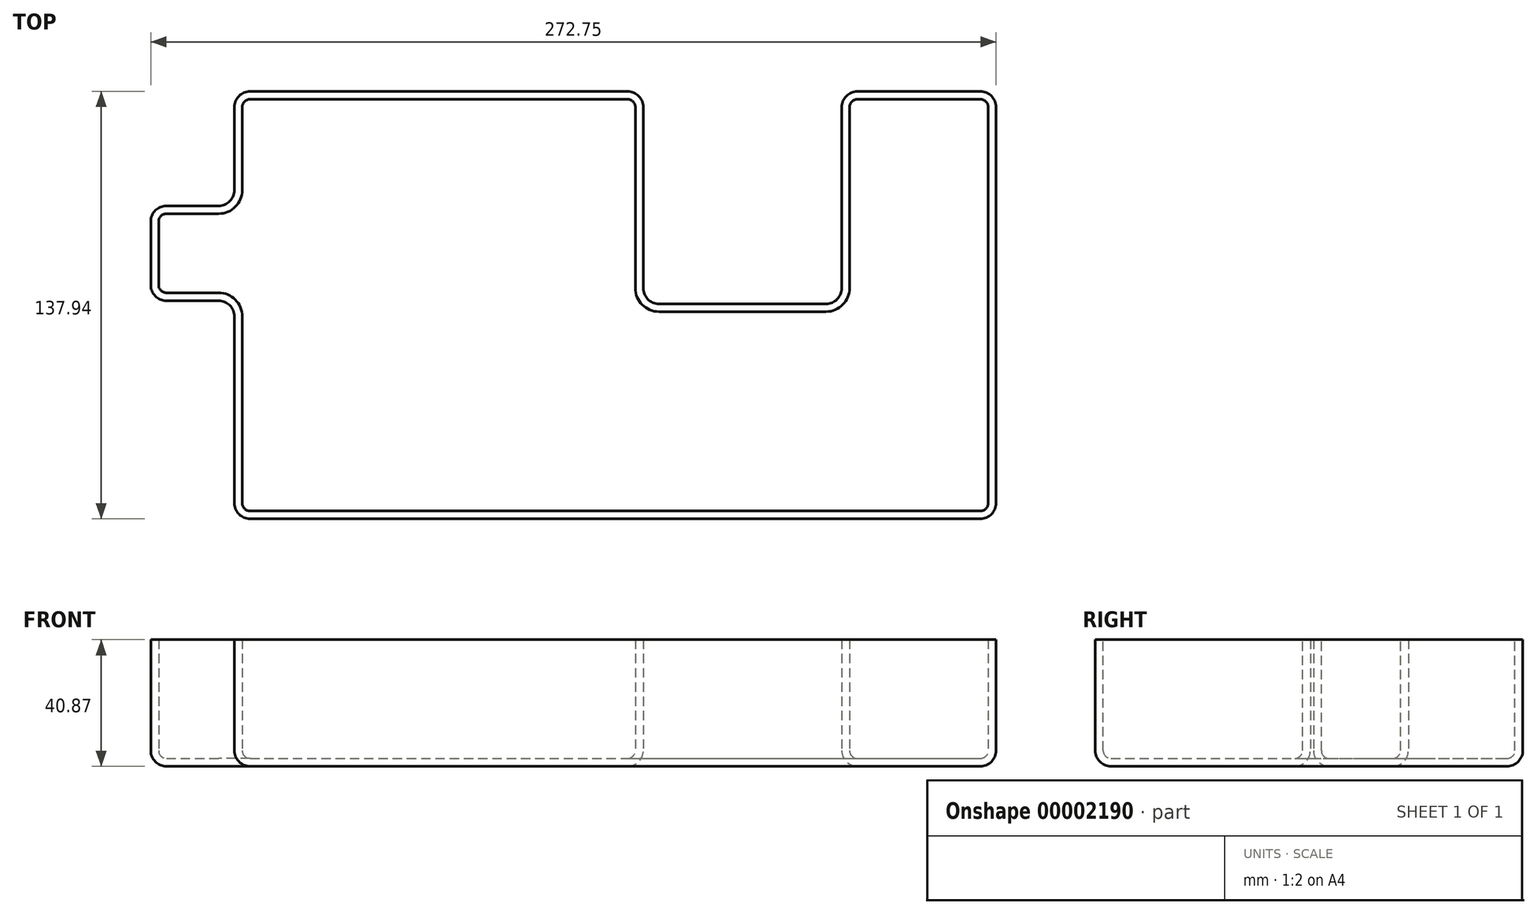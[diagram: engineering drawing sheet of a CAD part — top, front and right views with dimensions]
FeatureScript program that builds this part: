
annotation { "Feature Type Name" : "Feature", "Feature Type Description" : "" }
export const myFeature = defineFeature(function(context is Context, id is Id, definition is map)
    precondition{}
    {
        {
            var Q0;
            Q0=qCreatedBy(makeId("Top.planeOp"),FACE);
            var sketch = newSketch(context, id + "F0", { "sketchPlane" : qUnion([Q0])});
            skLineSegment(sketch, "E0.rect.bottom", {"start": v(-122.9, 68.97) * mm, "end": v(122.9, 68.97) * mm});
            skLineSegment(sketch, "E0.rect.top", {"start": v(-122.9, -68.97) * mm, "end": v(122.9, -68.97) * mm});
            skLineSegment(sketch, "E0.rect.left", {"start": v(-122.9, 68.97) * mm, "end": v(-122.9, -68.97) * mm});
            skLineSegment(sketch, "E0.rect.right", {"start": v(122.9, 68.97) * mm, "end": v(122.9, -68.97) * mm});
            skPoint(sketch, "E0.rect.middle", {"position": v(0, 0) * mm});
            skLineSegment(sketch, "E1.rect.bottom", {"start": v(-149.86, 32.04) * mm, "end": v(-95.92, 32.04) * mm});
            skLineSegment(sketch, "E1.rect.top", {"start": v(-149.86, 1.44) * mm, "end": v(-95.92, 1.44) * mm});
            skLineSegment(sketch, "E1.rect.left", {"start": v(-149.86, 32.04) * mm, "end": v(-149.86, 1.44) * mm});
            skLineSegment(sketch, "E1.rect.right", {"start": v(-95.92, 32.04) * mm, "end": v(-95.92, 1.44) * mm});
            skPoint(sketch, "E1.rect.middle", {"position": v(-122.9, 16.74) * mm});
            skLineSegment(sketch, "E2.rect.bottom", {"start": v(9.03, 113.83) * mm, "end": v(73.09, 113.83) * mm});
            skLineSegment(sketch, "E2.rect.top", {"start": v(9.03, 0.43) * mm, "end": v(73.09, 0.43) * mm});
            skLineSegment(sketch, "E2.rect.left", {"start": v(9.03, 113.83) * mm, "end": v(9.03, 0.43) * mm});
            skLineSegment(sketch, "E2.rect.right", {"start": v(73.09, 113.83) * mm, "end": v(73.09, 0.43) * mm});
            skPoint(sketch, "E2.rect.middle", {"position": v(41.06, 57.13) * mm});
            skSolve(sketch);
        }
        {
            var Q0;
            {var subQ0=sQuery(id+"F0.wireOp",EDGE,"E1.rect.left");Q0=makeQuery(id+"F0.imprint","IMPRINT",FACE,{"disambiguationData":[TD([[makeQuery(id+"F0.imprint","IMPRINT",EDGE,{"derivedFrom":subQ0}),1.0]])]});}
            var Q1;
            {var subQ0=sQuery(id+"F0.wireOp",EDGE,"E1.rect.right");Q1=makeQuery(id+"F0.imprint","IMPRINT",FACE,{"disambiguationData":[TD([[makeQuery(id+"F0.imprint","IMPRINT",EDGE,{"derivedFrom":subQ0}),-1.0]])]});}
            var Q2;
            {var subQ10=sQuery(id+"F0.wireOp",EDGE,"E0.rect.top");Q2=makeQuery(id+"F0.imprint","IMPRINT",FACE,{"disambiguationData":[TD([[makeQuery(id+"F0.imprint","IMPRINT",EDGE,{"derivedFrom":subQ10}),1.0]])]});}
            extrude(context, id + "F1", {"entities" : qUnion([Q0, Q1, Q2]), "depth" : 40.87 * mm});
        }
        {
            var Q0;
            Q0=makeQuery(id+"F1.opExtrude","SWEPT_EDGE",EDGE,{"disambiguationData":[OSD([sQuery(id+"F0.wireOp",EDGE,"E0.rect.top"),sQuery(id+"F0.wireOp",EDGE,"E0.rect.left")])]});
            var Q1;
            Q1=makeQuery(id+"F1.opExtrude","SWEPT_EDGE",EDGE,{"disambiguationData":[OSD([sQuery(id+"F0.wireOp",EDGE,"E1.rect.top"),sQuery(id+"F0.wireOp",EDGE,"E1.rect.left")])]});
            var Q2;
            Q2=makeQuery(id+"F1.opExtrude","SWEPT_EDGE",EDGE,{"disambiguationData":[OSD([sQuery(id+"F0.wireOp",EDGE,"E1.rect.bottom"),sQuery(id+"F0.wireOp",EDGE,"E1.rect.left")])]});
            var Q3;
            Q3=makeQuery(id+"F1.opExtrude","SWEPT_EDGE",EDGE,{"disambiguationData":[OSD([sQuery(id+"F0.wireOp",EDGE,"E0.rect.left"),sQuery(id+"F0.wireOp",EDGE,"E1.rect.bottom")])]});
            var Q4;
            Q4=makeQuery(id+"F1.opExtrude","SWEPT_EDGE",EDGE,{"disambiguationData":[OSD([sQuery(id+"F0.wireOp",EDGE,"E0.rect.bottom"),sQuery(id+"F0.wireOp",EDGE,"E0.rect.left")])]});
            var Q5;
            Q5=makeQuery(id+"F1.opExtrude","SWEPT_EDGE",EDGE,{"disambiguationData":[OSD([sQuery(id+"F0.wireOp",EDGE,"E0.rect.bottom"),sQuery(id+"F0.wireOp",EDGE,"E2.rect.left")])]});
            var Q6;
            Q6=makeQuery(id+"F1.opExtrude","SWEPT_EDGE",EDGE,{"disambiguationData":[OSD([sQuery(id+"F0.wireOp",EDGE,"E0.rect.bottom"),sQuery(id+"F0.wireOp",EDGE,"E2.rect.right")])]});
            var Q7;
            Q7=makeQuery(id+"F1.opExtrude","SWEPT_EDGE",EDGE,{"disambiguationData":[OSD([sQuery(id+"F0.wireOp",EDGE,"E2.rect.top"),sQuery(id+"F0.wireOp",EDGE,"E2.rect.right")])]});
            var Q8;
            Q8=makeQuery(id+"F1.opExtrude","SWEPT_EDGE",EDGE,{"disambiguationData":[OSD([sQuery(id+"F0.wireOp",EDGE,"E0.rect.bottom"),sQuery(id+"F0.wireOp",EDGE,"E0.rect.right")])]});
            var Q9;
            Q9=makeQuery(id+"F1.opExtrude","SWEPT_EDGE",EDGE,{"disambiguationData":[OSD([sQuery(id+"F0.wireOp",EDGE,"E0.rect.top"),sQuery(id+"F0.wireOp",EDGE,"E0.rect.right")])]});
            var Q10;
            Q10=makeQuery(id+"F1.opExtrude","SWEPT_EDGE",EDGE,{"disambiguationData":[OSD([sQuery(id+"F0.wireOp",EDGE,"E2.rect.top"),sQuery(id+"F0.wireOp",EDGE,"E2.rect.left")])]});
            var Q11;
            Q11=makeQuery(id+"F1.opExtrude","SWEPT_EDGE",EDGE,{"disambiguationData":[OSD([sQuery(id+"F0.wireOp",EDGE,"E0.rect.left"),sQuery(id+"F0.wireOp",EDGE,"E1.rect.top")])]});
            fillet(context, id + "F2", {"entities" : qUnion([Q0, Q1, Q2, Q3, Q4, Q5, Q6, Q7, Q8, Q9, Q10, Q11]), "radius" : 5.08 * mm, "tangentPropagation" : true, "allowEdgeOverflow" : false});
        }
        {
            var Q0;
            Q0=makeQuery(id+"F1.opExtrude","CAP_FACE",FACE,{"disambiguationData":[OSD([sQuery(id+"F0.wireOp",EDGE,"E0.rect.bottom"),sQuery(id+"F0.wireOp",EDGE,"E0.rect.top"),sQuery(id+"F0.wireOp",EDGE,"E0.rect.left"),sQuery(id+"F0.wireOp",EDGE,"E0.rect.right"),sQuery(id+"F0.wireOp",EDGE,"E1.rect.bottom"),sQuery(id+"F0.wireOp",EDGE,"E1.rect.top"),sQuery(id+"F0.wireOp",EDGE,"E1.rect.left"),sQuery(id+"F0.wireOp",EDGE,"E2.rect.top"),sQuery(id+"F0.wireOp",EDGE,"E2.rect.left"),sQuery(id+"F0.wireOp",EDGE,"E2.rect.right")])],"isStart":true});
            fillet(context, id + "F3", {"entities" : qUnion([Q0]), "radius" : 5.08 * mm, "tangentPropagation" : true, "allowEdgeOverflow" : false});
        }
        {
            var Q0;
            Q0=makeQuery(id+"F1.opExtrude","CAP_FACE",FACE,{"disambiguationData":[OSD([sQuery(id+"F0.wireOp",EDGE,"E0.rect.bottom"),sQuery(id+"F0.wireOp",EDGE,"E0.rect.top"),sQuery(id+"F0.wireOp",EDGE,"E0.rect.left"),sQuery(id+"F0.wireOp",EDGE,"E0.rect.right"),sQuery(id+"F0.wireOp",EDGE,"E1.rect.bottom"),sQuery(id+"F0.wireOp",EDGE,"E1.rect.top"),sQuery(id+"F0.wireOp",EDGE,"E1.rect.left"),sQuery(id+"F0.wireOp",EDGE,"E2.rect.top"),sQuery(id+"F0.wireOp",EDGE,"E2.rect.left"),sQuery(id+"F0.wireOp",EDGE,"E2.rect.right")])],"isStart":false});
            shell(context, id + "F4", {"entities" : qUnion([Q0]), "thickness" : 2.54 * mm});
        }
    });
